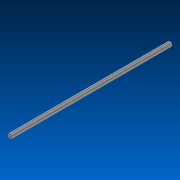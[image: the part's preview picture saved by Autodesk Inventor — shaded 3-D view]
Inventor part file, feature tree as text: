
AUTODESK INVENTOR PART (.ipt)
format: ipt  version: 2022.2 (Build 262287000, 287)  size: 121,344 bytes
history: native  units: in
note: dims shown in document units (in); Inventor stores cm internally (conversion verified against a paired STEP export)
features: extrude x1, sketch x1, other x1
ambient origin geometry x8: Origin, YZ Plane, XZ Plane, XY Plane, X Axis, Y Axis, Z Axis, Center Point
bodies: Solid1 (feature_tree)
feature tree (3):
  extrude  "Extrusion1"  TaperAngle=0.0deg  [1 undecoded]
  sketch  "Sketch1"  dims[d0=16.0in d1=0.0in]
  other  "Cut-Extrude2"
note: 1 required parameter value undecoded (feature->parameter linkage not recoverable at this tier; creation-order binding heuristic only, values carry confidence <= 0.55)
